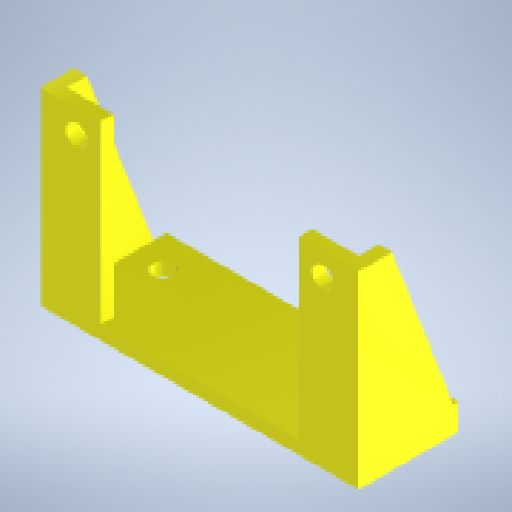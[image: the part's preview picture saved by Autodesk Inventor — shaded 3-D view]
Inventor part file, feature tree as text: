
AUTODESK INVENTOR PART (.ipt)
format: ipt  version: 2025.3 (Build 293356000, 356)  size: 171,008 bytes
history: native  units: mm
features: sketch x4, extrude x3, other x1, mirror x1, hole x1
ambient origin geometry x8: Origin, YZ Plane, XZ Plane, XY Plane, X Axis, Y Axis, Z Axis, Center Point
bodies: Body1 (feature_tree)
feature tree (10):
  other  "ソリッド1"
  extrude  "土台"  Depth=44.0mm
  extrude  "モータ支柱"  Depth=17.0mm
  extrude  "補強リブ"  Depth=2.0mm TaperAngle=0.0deg
  mirror  "ミラー1"
  hole  "穴1"  [1 undecoded]
  sketch  "スケッチ1"
  sketch  "スケッチ2"
  sketch  "スケッチ3"
  sketch  "スケッチ4"
note: 1 required parameter value undecoded (feature->parameter linkage not recoverable at this tier; creation-order binding heuristic only, values carry confidence <= 0.55)
